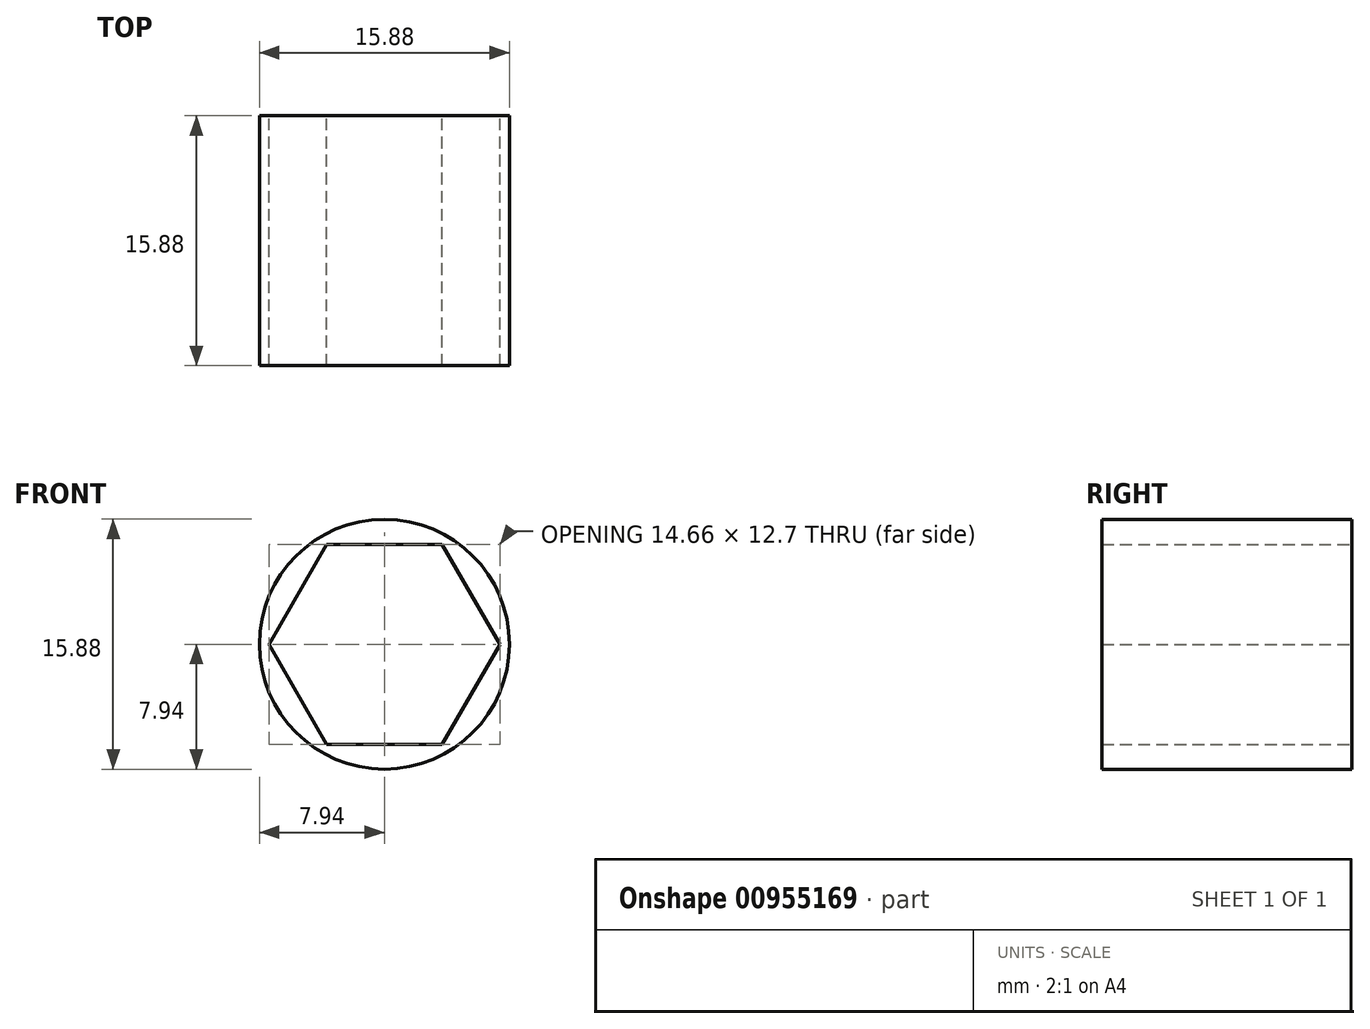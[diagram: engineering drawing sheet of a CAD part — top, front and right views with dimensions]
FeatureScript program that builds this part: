
annotation { "Feature Type Name" : "Feature", "Feature Type Description" : "" }
export const myFeature = defineFeature(function(context is Context, id is Id, definition is map)
    precondition{}
    {
        {
            var Q0;
            Q0=qCreatedBy(makeId("Front.planeOp"),FACE);
            var sketch = newSketch(context, id + "F0", { "sketchPlane" : qUnion([Q0])});
            skCircle(sketch, "E0", {"center": v(0, 0) * mm, "radius": 7.94 * mm});
            skCircle(sketch, "E1.cCircle", {"center": v(0, 0) * mm, "radius": 6.35 * mm, "construction": true});
            skLineSegment(sketch, "E1.0", {"start": v(-3.67, 6.35) * mm, "end": v(3.67, 6.35) * mm});
            skLineSegment(sketch, "E1.1", {"start": v(3.67, 6.35) * mm, "end": v(7.33, 0) * mm});
            skLineSegment(sketch, "E1.2", {"start": v(7.33, 0) * mm, "end": v(3.67, -6.35) * mm});
            skLineSegment(sketch, "E1.3", {"start": v(3.67, -6.35) * mm, "end": v(-3.67, -6.35) * mm});
            skLineSegment(sketch, "E1.4", {"start": v(-3.67, -6.35) * mm, "end": v(-7.33, 0) * mm});
            skLineSegment(sketch, "E1.5", {"start": v(-7.33, 0) * mm, "end": v(-3.67, 6.35) * mm});
            skPoint(sketch, "E1.0.midPoint", {"position": v(0, 6.35) * mm});
            skSolve(sketch);
        }
        {
            var Q0;
            Q0=qSketchRegion(id+"F0",true);
            extrude(context, id + "F1", {"entities" : qUnion([Q0]), "depth" : 15.88 * mm, "offsetDistance" : 25.4 * mm});
        }
    });
